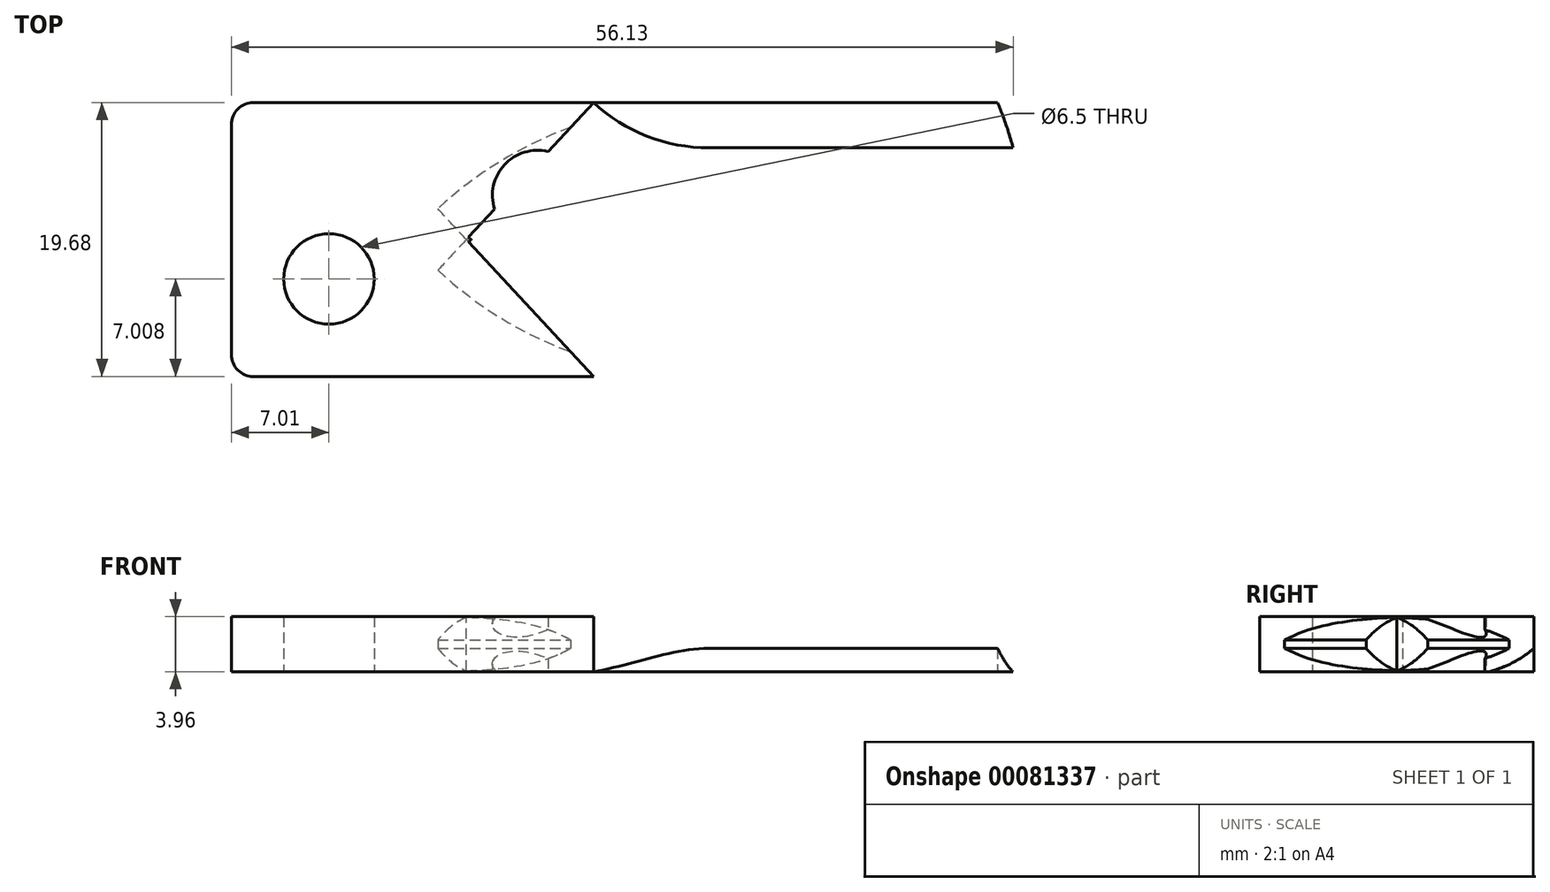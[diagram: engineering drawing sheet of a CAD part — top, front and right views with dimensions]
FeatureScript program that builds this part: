
annotation { "Feature Type Name" : "Feature", "Feature Type Description" : "" }
export const myFeature = defineFeature(function(context is Context, id is Id, definition is map)
    precondition{}
    {
        {
            var Q0;
            Q0=qCreatedBy(makeId("Top.planeOp"),FACE);
            var sketch = newSketch(context, id + "F0", { "sketchPlane" : qUnion([Q0])});
            skLineSegment(sketch, "E0", {"start": v(0, 8.26) * mm, "end": v(0, -8.26) * mm});
            skLineSegment(sketch, "E1", {"start": v(1.59, -9.84) * mm, "end": v(55.01, -9.84) * mm});
            skArc(sketch, "E2", {"start": v(55.01, -9.84) * mm, "mid": v(57, 0) * mm, "end": v(55.01, 9.84) * mm});
            skLineSegment(sketch, "E3", {"start": v(55.01, 9.84) * mm, "end": v(1.59, 9.84) * mm});
            skPoint(sketch, "E4.visualSharp", {"position": v(0, 9.84) * mm});
            skArc(sketch, "E4.filletArc", {"start": v(1.59, 9.84) * mm, "mid": v(0.46, 9.38) * mm, "end": v(0, 8.26) * mm});
            skPoint(sketch, "E5.visualSharp", {"position": v(0, -9.84) * mm});
            skArc(sketch, "E5.filletArc", {"start": v(0, -8.26) * mm, "mid": v(0.46, -9.38) * mm, "end": v(1.59, -9.84) * mm});
            skCircle(sketch, "E6", {"center": v(7.01, -2.83) * mm, "radius": 3.25 * mm});
            skCircle(sketch, "E7", {"center": v(22, 3.16) * mm, "radius": 3.25 * mm});
            skLineSegment(sketch, "E8", {"start": v(34.3, 6.6) * mm, "end": v(60.85, 6.6) * mm});
            skArc(sketch, "E9", {"start": v(26, 9.84) * mm, "mid": v(29.84, 7.43) * mm, "end": v(34.3, 6.6) * mm});
            skLineSegment(sketch, "E10.MirrorCS", {"start": v(34.3, -6.6) * mm, "end": v(60.85, -6.6) * mm});
            skArc(sketch, "E11.MirrorCS", {"start": v(26, -9.84) * mm, "mid": v(29.84, -7.43) * mm, "end": v(34.3, -6.6) * mm});
            skSolve(sketch);
        }
        {
            var Q0;
            Q0=makeQuery(id+"F0.imprint","IMPRINT",FACE,{"disambiguationData":[TD([[makeQuery(id+"F0.imprint","IMPRINT",EDGE,{"derivedFrom":sQuery(id+"F0.wireOp",EDGE,"E0")}),1.0]])]});
            var Q1;
            {var subQ5=sQuery(id+"F0.wireOp",EDGE,"E9");Q1=makeQuery(id+"F0.imprint","IMPRINT",FACE,{"disambiguationData":[TD([[makeQuery(id+"F0.imprint","IMPRINT",EDGE,{"derivedFrom":subQ5}),1.0]])]});}
            var Q2;
            {var subQ3=sQuery(id+"F0.wireOp",EDGE,"E11.MirrorCS");Q2=makeQuery(id+"F0.imprint","IMPRINT",FACE,{"disambiguationData":[TD([[makeQuery(id+"F0.imprint","IMPRINT",EDGE,{"derivedFrom":subQ3}),-1.0]])]});}
            extrude(context, id + "F1", {"entities" : qUnion([Q0, Q1, Q2]), "depth" : 3.96 * mm, "offsetDistance" : 25.4 * mm});
        }
        {
            var Q0;
            Q0=qCreatedBy(makeId("Right.planeOp"),FACE);
            cPlane(context, id + "F2", {"entities" : qUnion([Q0]), "cplaneType" : CPlaneType.OFFSET, "offset" : 57 * mm, "width" : 152.4 * mm, "height" : 152.4 * mm});
        }
        {
            var Q0;
            Q0=qCreatedBy(id+"F2.planeOp",FACE);
            var sketch = newSketch(context, id + "F3", { "sketchPlane" : qUnion([Q0])});
            skLineSegment(sketch, "E12.0.0", {"start": v(-9.84, 0) * mm, "end": v(9.84, 0) * mm, "construction": true});
            skLineSegment(sketch, "E12.0.1", {"start": v(9.84, 0) * mm, "end": v(9.84, 3.96) * mm, "construction": true});
            skLineSegment(sketch, "E12.0.2", {"start": v(9.84, 3.96) * mm, "end": v(-9.84, 3.96) * mm, "construction": true});
            skLineSegment(sketch, "E12.0.3", {"start": v(-9.84, 3.96) * mm, "end": v(-9.84, 0) * mm, "construction": true});
            skArc(sketch, "E13", {"start": v(9.84, 2.29) * mm, "mid": v(8.31, 3.31) * mm, "end": v(6.6, 3.96) * mm});
            skLineSegment(sketch, "E14", {"start": v(-9.84, 1.98) * mm, "end": v(9.84, 1.98) * mm, "construction": true});
            skArc(sketch, "E15.MirrorCS", {"start": v(9.84, 1.68) * mm, "mid": v(8.31, 0.65) * mm, "end": v(6.6, 0) * mm});
            skArc(sketch, "E16.MirrorCS", {"start": v(-9.84, 2.29) * mm, "mid": v(-8.31, 3.31) * mm, "end": v(-6.6, 3.96) * mm});
            skArc(sketch, "E17.MirrorCS", {"start": v(-9.84, 1.68) * mm, "mid": v(-8.31, 0.65) * mm, "end": v(-6.6, 0) * mm});
            skLineSegment(sketch, "E18", {"start": v(-6.6, 0) * mm, "end": v(6.6, 0) * mm});
            skLineSegment(sketch, "E19", {"start": v(6.6, 3.96) * mm, "end": v(-6.6, 3.96) * mm});
            skLineSegment(sketch, "E20", {"start": v(-9.84, 2.29) * mm, "end": v(-9.84, 1.68) * mm});
            skLineSegment(sketch, "E21", {"start": v(9.84, 1.68) * mm, "end": v(9.84, 2.29) * mm});
            skLineSegment(sketch, "E22.bottom", {"start": v(-13.03, -3.18) * mm, "end": v(13.02, -3.18) * mm});
            skLineSegment(sketch, "E22.top", {"start": v(-13.03, 7.14) * mm, "end": v(13.02, 7.14) * mm});
            skLineSegment(sketch, "E22.left", {"start": v(-13.03, -3.18) * mm, "end": v(-13.03, 7.14) * mm});
            skLineSegment(sketch, "E22.right", {"start": v(13.02, -3.17) * mm, "end": v(13.02, 7.14) * mm});
            skLineSegment(sketch, "E23", {"start": v(6.6, 3.96) * mm, "end": v(6.6, 7.14) * mm});
            skLineSegment(sketch, "E24", {"start": v(9.84, 2.29) * mm, "end": v(13.02, 2.29) * mm});
            skLineSegment(sketch, "E25", {"start": v(9.84, 1.68) * mm, "end": v(13.02, 1.68) * mm});
            skLineSegment(sketch, "E26", {"start": v(6.6, 0) * mm, "end": v(6.6, -3.18) * mm});
            skLineSegment(sketch, "E27", {"start": v(-6.6, 3.96) * mm, "end": v(-6.6, 7.14) * mm});
            skLineSegment(sketch, "E28", {"start": v(-9.84, 2.29) * mm, "end": v(-13.03, 2.29) * mm});
            skLineSegment(sketch, "E29", {"start": v(-9.84, 1.68) * mm, "end": v(-13.03, 1.68) * mm});
            skLineSegment(sketch, "E30", {"start": v(-6.6, 0) * mm, "end": v(-6.6, -3.18) * mm});
            skSolve(sketch);
        }
        {
            var Q0;
            Q0=makeQuery(id+"F3.imprint","IMPRINT",FACE,{"disambiguationData":[TD([[makeQuery(id+"F3.imprint","IMPRINT",EDGE,{"derivedFrom":sQuery(id+"F3.wireOp",EDGE,"E15.MirrorCS")}),1.0]])]});
            var Q1;
            Q1=makeQuery(id+"F3.imprint","IMPRINT",FACE,{"disambiguationData":[TD([[makeQuery(id+"F3.imprint","IMPRINT",EDGE,{"derivedFrom":sQuery(id+"F3.wireOp",EDGE,"E13")}),-1.0]])]});
            var Q2;
            Q2=sQuery(id+"F0.wireOp",EDGE,"E8");
            var Q3;
            Q3=sQuery(id+"F0.wireOp",EDGE,"E9");
            sweep(context, id + "F4", {"operationType" : NewBodyOperationType.REMOVE, "profiles" : qUnion([Q0, Q1]), "path" : qUnion([Q2, Q3])});
        }
        {
            var Q0;
            Q0=makeQuery(id+"F3.imprint","IMPRINT",FACE,{"disambiguationData":[TD([[makeQuery(id+"F3.imprint","IMPRINT",EDGE,{"derivedFrom":sQuery(id+"F3.wireOp",EDGE,"E17.MirrorCS")}),-1.0]])]});
            var Q1;
            Q1=makeQuery(id+"F3.imprint","IMPRINT",FACE,{"disambiguationData":[TD([[makeQuery(id+"F3.imprint","IMPRINT",EDGE,{"derivedFrom":sQuery(id+"F3.wireOp",EDGE,"E16.MirrorCS")}),1.0]])]});
            var Q2;
            Q2=sQuery(id+"F0.wireOp",EDGE,"E10.MirrorCS");
            var Q3;
            Q3=sQuery(id+"F0.wireOp",EDGE,"E11.MirrorCS");
            sweep(context, id + "F5", {"operationType" : NewBodyOperationType.REMOVE, "profiles" : qUnion([Q0, Q1]), "path" : qUnion([Q2, Q3])});
        }
    });
